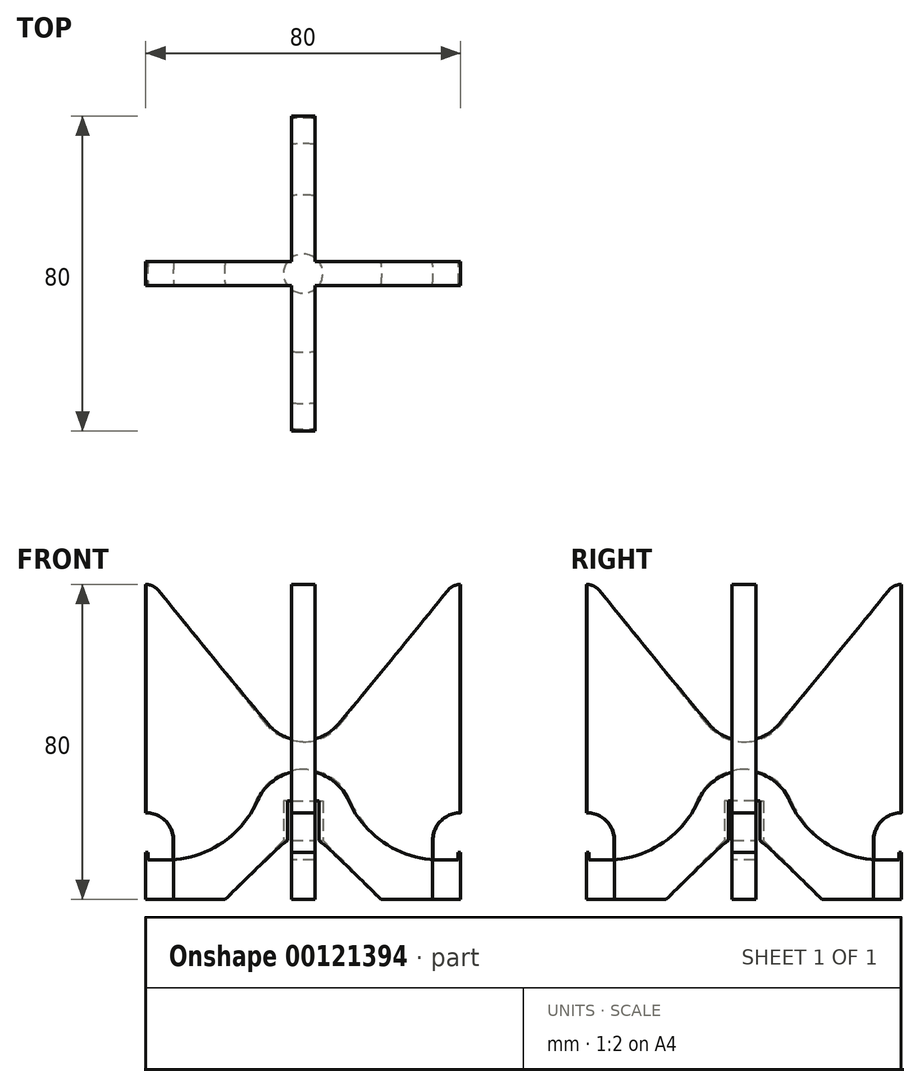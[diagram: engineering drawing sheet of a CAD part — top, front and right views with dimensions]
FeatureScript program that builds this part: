
annotation { "Feature Type Name" : "Feature", "Feature Type Description" : "" }
export const myFeature = defineFeature(function(context is Context, id is Id, definition is map)
    precondition{}
    {
        {
            var Q0;
            Q0=qCreatedBy(makeId("Front.planeOp"),FACE);
            var sketch = newSketch(context, id + "F0", { "sketchPlane" : qUnion([Q0])});
            skLineSegment(sketch, "E0", {"start": v(0, 0) * mm, "end": v(50.5, 0) * mm});
            skLineSegment(sketch, "E1", {"start": v(50.5, 0) * mm, "end": v(50.5, 10) * mm});
            skLineSegment(sketch, "E2", {"start": v(50.5, 10) * mm, "end": v(48.5, 10) * mm});
            skLineSegment(sketch, "E3", {"start": v(42.5, 10) * mm, "end": v(42.5, 12) * mm});
            skLineSegment(sketch, "E4", {"start": v(42.5, 12) * mm, "end": v(39.5, 12) * mm});
            skLineSegment(sketch, "E5", {"start": v(39.5, 12) * mm, "end": v(39.5, 10) * mm});
            skLineSegment(sketch, "E6", {"start": v(39.5, 10) * mm, "end": v(34.91, 10) * mm});
            skArc(sketch, "E7", {"start": v(42.5, 10) * mm, "mid": v(45.5, 7) * mm, "end": v(48.5, 10) * mm});
            skArc(sketch, "E8", {"start": v(11.94, 25.13) * mm, "mid": v(7.15, 30.86) * mm, "end": v(0, 33) * mm});
            skArc(sketch, "E9", {"start": v(11.94, 25.13) * mm, "mid": v(21.16, 14.12) * mm, "end": v(34.91, 10) * mm});
            skLineSegment(sketch, "E10", {"start": v(0, 33) * mm, "end": v(0, 43.34) * mm});
            skLineSegment(sketch, "E11", {"start": v(0, 33) * mm, "end": v(0, 0) * mm});
            skLineSegment(sketch, "E12", {"start": v(0, 25) * mm, "end": v(5, 25) * mm});
            skLineSegment(sketch, "E13", {"start": v(5, 25) * mm, "end": v(5, 15) * mm});
            skLineSegment(sketch, "E14", {"start": v(5, 15) * mm, "end": v(20, 0) * mm});
            skSolve(sketch);
        }
        {
            var Q0;
            {var subQ1=sQuery(id+"F0.wireOp",EDGE,"E1");Q0=makeQuery(id+"F0.imprint","IMPRINT",FACE,{"disambiguationData":[TD([[makeQuery(id+"F0.imprint","IMPRINT",EDGE,{"derivedFrom":subQ1}),1.0]])]});}
            var Q1;
            {var subQ0=sQuery(id+"F0.wireOp",EDGE,"E12");Q1=makeQuery(id+"F0.imprint","IMPRINT",FACE,{"disambiguationData":[TD([[makeQuery(id+"F0.imprint","IMPRINT",EDGE,{"derivedFrom":subQ0}),-1.0]])]});}
            var Q2;
            Q2=sQuery(id+"F0.wireOp",EDGE,"E11");
            revolve(context, id + "F1", {"entities" : qUnion([Q0, Q1]), "axis" : qUnion([Q2]), "revolveType" : RevolveType.FULL});
        }
        {
            var Q0;
            Q0=qCreatedBy(makeId("Front.planeOp"),FACE);
            var sketch = newSketch(context, id + "F2", { "sketchPlane" : qUnion([Q0])});
            skLineSegment(sketch, "E15", {"start": v(0, 0) * mm, "end": v(33, 0) * mm});
            skLineSegment(sketch, "E16", {"start": v(33, 0) * mm, "end": v(33, 15) * mm});
            skLineSegment(sketch, "E17", {"start": v(40, 22) * mm, "end": v(40, 22) * mm});
            skLineSegment(sketch, "E18", {"start": v(40, 22) * mm, "end": v(40, 80) * mm});
            skLineSegment(sketch, "E19", {"start": v(0, 40) * mm, "end": v(0, 0) * mm});
            skArc(sketch, "E20", {"start": v(0, 40) * mm, "mid": v(5.17, 41.17) * mm, "end": v(9.33, 44.45) * mm});
            skArc(sketch, "E21", {"start": v(40, 80) * mm, "mid": v(38.28, 79.6) * mm, "end": v(36.9, 78.52) * mm});
            skLineSegment(sketch, "E22", {"start": v(9.33, 44.45) * mm, "end": v(36.9, 78.52) * mm});
            skPoint(sketch, "E23.visualSharp", {"position": v(33, 22) * mm});
            skArc(sketch, "E23.filletArc", {"start": v(40, 22) * mm, "mid": v(35.05, 19.95) * mm, "end": v(33, 15) * mm});
            skSolve(sketch);
        }
        {
            var Q0;
            Q0=makeQuery(id+"F2.imprint","IMPRINT",FACE,{"disambiguationData":[TD([[makeQuery(id+"F2.imprint","IMPRINT",EDGE,{"derivedFrom":sQuery(id+"F2.wireOp",EDGE,"E15")}),1.0]])]});
            var Q1;
            Q1=sQuery(id+"F2.wireOp",EDGE,"E19");
            revolve(context, id + "F3", {"entities" : qUnion([Q0]), "axis" : qUnion([Q1]), "revolveType" : RevolveType.FULL});
        }
        {
            var Q0;
            Q0=qCreatedBy(makeId("Top.planeOp"),FACE);
            var sketch = newSketch(context, id + "F4", { "sketchPlane" : qUnion([Q0])});
            skLineSegment(sketch, "E24.bottom", {"start": v(40, -3) * mm, "end": v(-40, -3) * mm});
            skLineSegment(sketch, "E24.top", {"start": v(40, 3) * mm, "end": v(-40, 3) * mm});
            skLineSegment(sketch, "E24.left", {"start": v(40, -3) * mm, "end": v(40, 3) * mm});
            skLineSegment(sketch, "E24.right", {"start": v(-40, -3) * mm, "end": v(-40, 3) * mm});
            skPoint(sketch, "E24.middle", {"position": v(0, 0) * mm});
            skLineSegment(sketch, "E25.bottom", {"start": v(3, -40) * mm, "end": v(-3, -40) * mm});
            skLineSegment(sketch, "E25.top", {"start": v(3, 40) * mm, "end": v(-3, 40) * mm});
            skLineSegment(sketch, "E25.left", {"start": v(3, -40) * mm, "end": v(3, 40) * mm});
            skLineSegment(sketch, "E25.right", {"start": v(-3, -40) * mm, "end": v(-3, 40) * mm});
            skSolve(sketch);
        }
        {
            var Q0;
            Q0 = qSketchRegion(id + "F4", true);
            extrude(context, id + "F5", {"entities" : qUnion([Q0]), "operationType" : NewBodyOperationType.INTERSECT, "endBound" : BoundingType.THROUGH_ALL, "depth" : 25 * mm});
        }
        {
            var Q0;
            {var subQ0=sQuery(id+"F0.wireOp",EDGE,"E12");Q0=makeQuery(id+"F0.imprint","IMPRINT",FACE,{"disambiguationData":[TD([[makeQuery(id+"F0.imprint","IMPRINT",EDGE,{"derivedFrom":subQ0}),-1.0]])]});}
            var Q1;
            Q1=sQuery(id+"F0.wireOp",EDGE,"E11");
            revolve(context, id + "F6", {"operationType" : NewBodyOperationType.REMOVE, "entities" : qUnion([Q0]), "axis" : qUnion([Q1]), "revolveType" : RevolveType.FULL, "oppositeDirection" : true});
        }
    });
